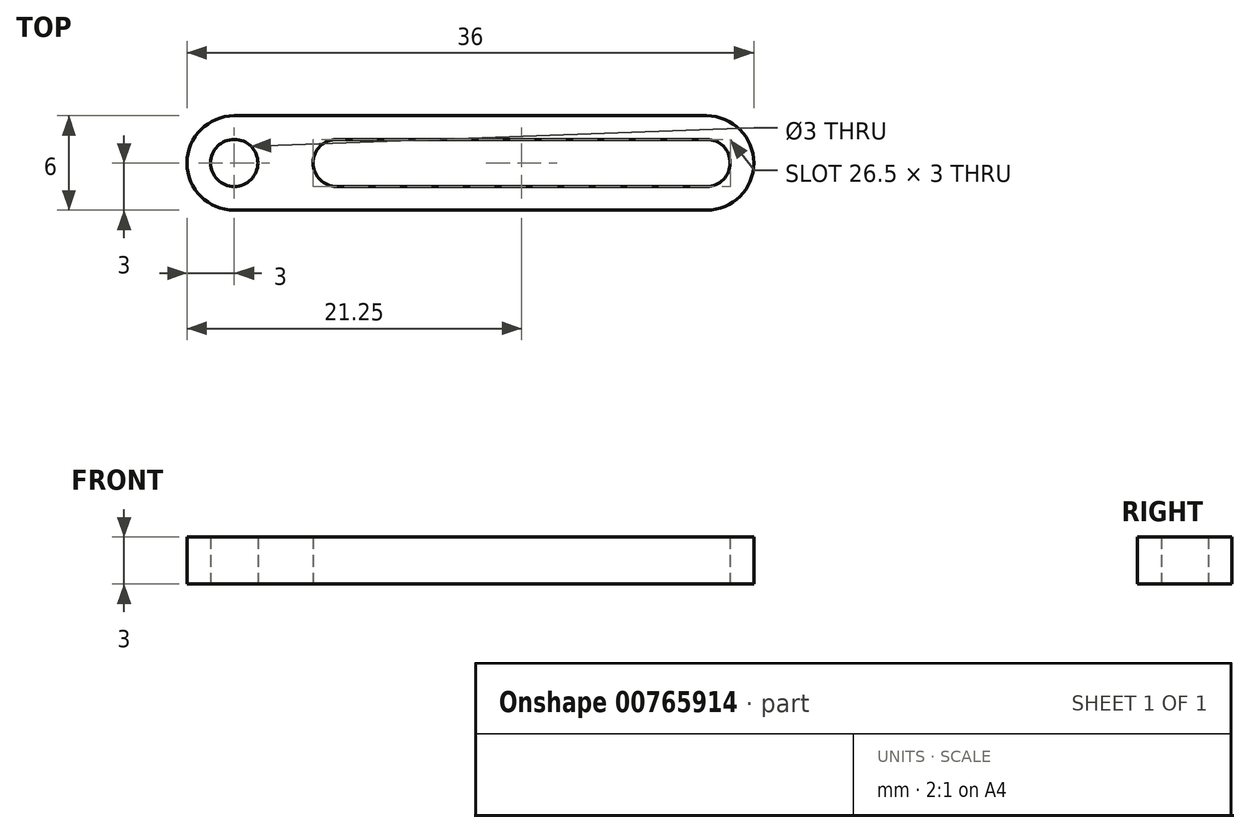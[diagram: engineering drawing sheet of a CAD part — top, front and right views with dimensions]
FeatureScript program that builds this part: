
annotation { "Feature Type Name" : "Feature", "Feature Type Description" : "" }
export const myFeature = defineFeature(function(context is Context, id is Id, definition is map)
    precondition{}
    {
        {
            var Q0;
            Q0=qCreatedBy(makeId("Top.planeOp"),FACE);
            var sketch = newSketch(context, id + "F0", { "sketchPlane" : qUnion([Q0])});
            skLineSegment(sketch, "E0", {"start": v(0, 0) * mm, "end": v(0, 26.48) * mm, "construction": true});
            skLineSegment(sketch, "E1", {"start": v(0, 3) * mm, "end": v(-15, 3) * mm});
            skCircle(sketch, "E2", {"center": v(-15, 0) * mm, "radius": 1.5 * mm});
            skCircle(sketch, "E3", {"center": v(-15, 0) * mm, "radius": 3 * mm});
            skCircle(sketch, "E4", {"center": v(-8.5, 0) * mm, "radius": 1.5 * mm});
            skLineSegment(sketch, "E5", {"start": v(-15, -3) * mm, "end": v(0, -3) * mm});
            skLineSegment(sketch, "E6.MirrorCS", {"start": v(15, -3) * mm, "end": v(0, -3) * mm});
            skCircle(sketch, "E7.MirrorC", {"center": v(15, 0) * mm, "radius": 1.5 * mm});
            skLineSegment(sketch, "E8.MirrorCS", {"start": v(0, 3) * mm, "end": v(15, 3) * mm});
            skArc(sketch, "E9", {"start": v(15, 3) * mm, "mid": v(18, 0) * mm, "end": v(15, -3) * mm});
            skLineSegment(sketch, "E10", {"start": v(-8.5, 1.5) * mm, "end": v(15, 1.5) * mm});
            skLineSegment(sketch, "E11", {"start": v(15, -1.5) * mm, "end": v(-8.5, -1.5) * mm});
            skSolve(sketch);
        }
        {
            var Q0;
            {var subQ5=sQuery(id+"F0.wireOp",EDGE,"E1");Q0=makeQuery(id+"F0.imprint","IMPRINT",FACE,{"disambiguationData":[TD([[makeQuery(id+"F0.imprint","IMPRINT",EDGE,{"derivedFrom":subQ5}),1.0]])]});}
            var Q1;
            Q1=makeQuery(id+"F0.imprint","IMPRINT",FACE,{"disambiguationData":[TD([[makeQuery(id+"F0.imprint","IMPRINT",EDGE,{"derivedFrom":sQuery(id+"F0.wireOp",EDGE,"E2")}),-1.0]])]});
            extrude(context, id + "F1", {"entities" : qUnion([Q0, Q1]), "depth" : 3 * mm, "offsetDistance" : 25 * mm});
        }
    });
